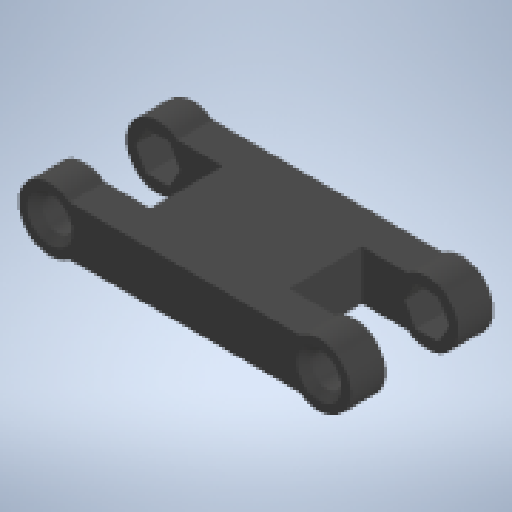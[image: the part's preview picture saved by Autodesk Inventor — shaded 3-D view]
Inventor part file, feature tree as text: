
AUTODESK INVENTOR PART (.ipt)
format: ipt  version: 2025.2 (Build 292293000, 293)  size: 196,096 bytes
history: native  units: mm
features: sketch x5, extrude x3, other x2, hole x2
ambient origin geometry x8: Origin, YZ Plane, XZ Plane, XY Plane, X Axis, Y Axis, Z Axis, Center Point
bodies: Body1 (feature_tree)
feature tree (12):
  other  "Barra1_0001_001"
  other  "Sólido1"
  extrude  "Extrusão1"  Depth=2.75mm
  extrude  "Extrusão2"  Depth=14.9075mm
  hole  "Furo1"  [1 undecoded]
  hole  "Furo2"  [1 undecoded]
  extrude  "Extrusão3"  Depth=15.430721mm
  sketch  "Esboço1"  dims[d5=2.75mm d6=2.75mm]
  sketch  "Esboço2"  dims[d7=7.0mm d9=14.9075mm]
  sketch  "Esboço3"  dims[d11=29.815mm d12=5.0mm]
  sketch  "Esboço4"  dims[d13=5.0mm d14=3.9mm d15=0.0mm]
  sketch  "Esboço5"  dims[d16=8.04mm d17=0.0mm d21=15.430721mm d23=3.5mm d24=6.0mm d25=5.0mm d26=2.0mm d27=14.3117mm d28=8.0mm d29=20.594885mm d30=3.5mm d31=6.0mm d32=5.0mm d33=2.0mm d34=14.3117mm d35=8.0mm d36=20.594885mm d37=7.0mm d40=3.9mm d41=0.0mm d22=0.5mm d42=0.0mm d43=0.0mm d44=0.0mm d45=0.0mm]
note: 2 required parameter values undecoded (feature->parameter linkage not recoverable at this tier; creation-order binding heuristic only, values carry confidence <= 0.55)
